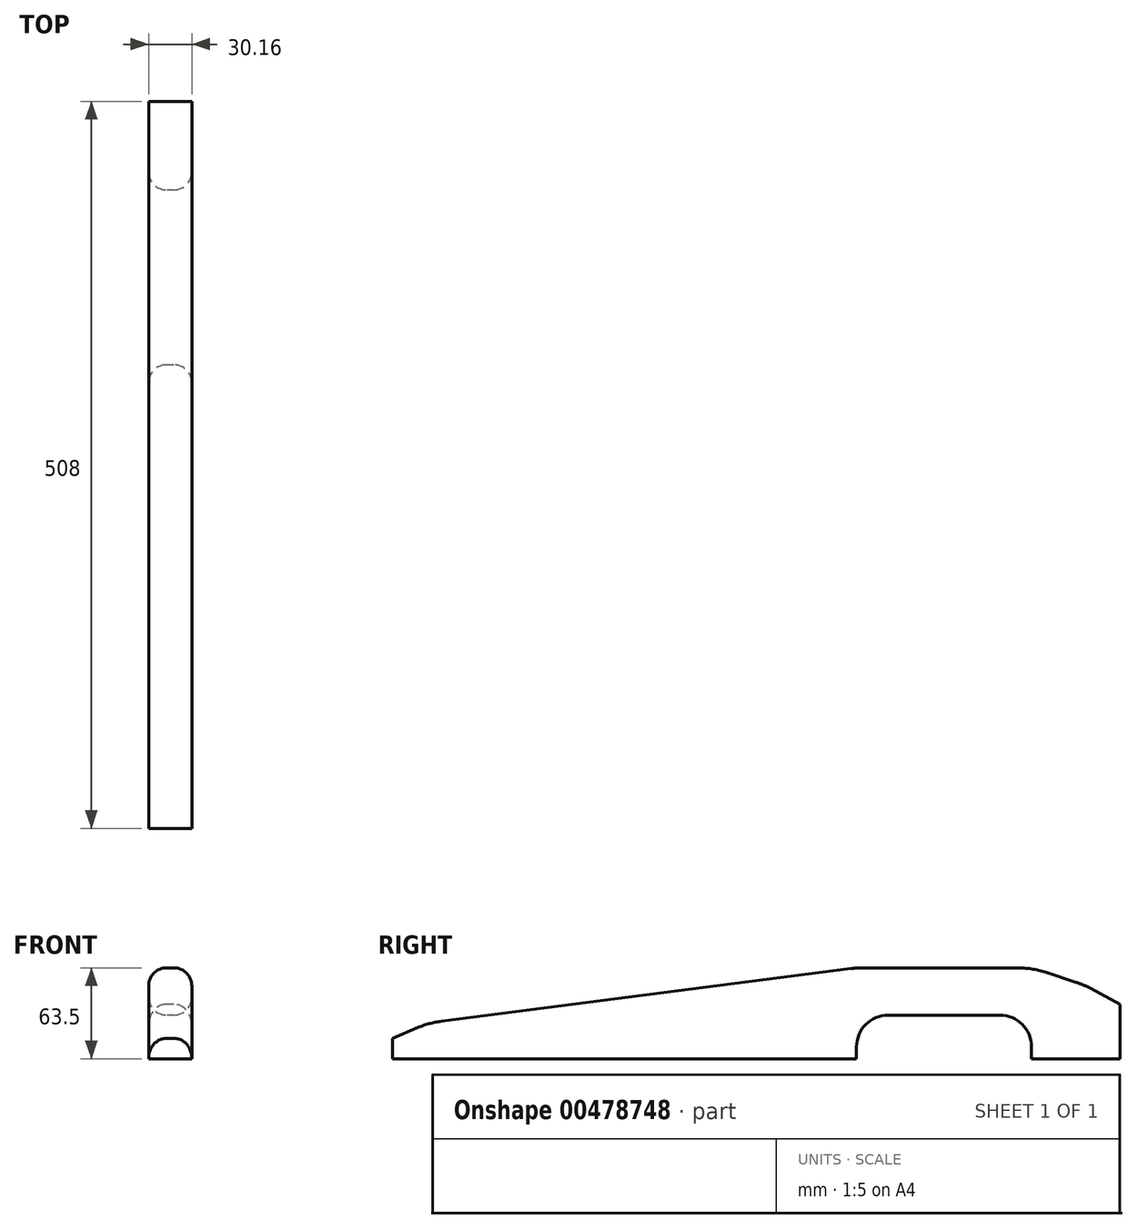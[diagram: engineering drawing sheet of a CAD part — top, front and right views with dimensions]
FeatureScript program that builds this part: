
annotation { "Feature Type Name" : "Feature", "Feature Type Description" : "" }
export const myFeature = defineFeature(function(context is Context, id is Id, definition is map)
    precondition{}
    {
        {
            var Q0;
            Q0=qCreatedBy(makeId("Right.planeOp"),FACE);
            var sketch = newSketch(context, id + "F0", { "sketchPlane" : qUnion([Q0])});
            skLineSegment(sketch, "E0.bottom", {"start": v(0, 0) * mm, "end": v(323.85, 0) * mm});
            skLineSegment(sketch, "E0.top", {"start": v(323.85, 63.5) * mm, "end": v(446.09, 63.5) * mm});
            skLineSegment(sketch, "E0.left", {"start": v(0, 0) * mm, "end": v(0, 14.29) * mm});
            skLineSegment(sketch, "E0.right", {"start": v(508, 0) * mm, "end": v(508, 38.1) * mm});
            skPoint(sketch, "E1", {"position": v(323.85, 0) * mm});
            skPoint(sketch, "E2", {"position": v(446.09, 0) * mm});
            skPoint(sketch, "E3", {"position": v(508, 38.1) * mm});
            skPoint(sketch, "E4", {"position": v(0, 14.29) * mm});
            skLineSegment(sketch, "E5", {"start": v(323.85, 0) * mm, "end": v(323.85, 30.48) * mm});
            skLineSegment(sketch, "E6", {"start": v(323.85, 30.48) * mm, "end": v(446.09, 30.48) * mm});
            skLineSegment(sketch, "E7", {"start": v(446.09, 30.48) * mm, "end": v(446.09, 0) * mm});
            skLineSegment(sketch, "E8.trimOffspring", {"start": v(446.09, 0) * mm, "end": v(508, 0) * mm});
            skLineSegment(sketch, "E9", {"start": v(0, 14.29) * mm, "end": v(25.4, 25.07) * mm});
            skLineSegment(sketch, "E10", {"start": v(25.4, 25.07) * mm, "end": v(323.85, 63.5) * mm});
            skLineSegment(sketch, "E11", {"start": v(508, 38.1) * mm, "end": v(482.6, 51.6) * mm});
            skLineSegment(sketch, "E12", {"start": v(482.6, 51.6) * mm, "end": v(446.09, 63.5) * mm});
            skSolve(sketch);
        }
        {
            var Q0;
            Q0=makeQuery(id+"F0.imprint","IMPRINT",FACE,{"disambiguationData":[TD([[makeQuery(id+"F0.imprint","IMPRINT",EDGE,{"derivedFrom":sQuery(id+"F0.wireOp",EDGE,"E0.bottom")}),1.0]])]});
            extrude(context, id + "F1", {"entities" : qUnion([Q0]), "depth" : 15.08 * mm, "hasSecondDirection" : true, "secondDirectionOppositeDirection" : true, "secondDirectionDepth" : 15.08 * mm});
        }
        {
            var Q0;
            Q0=makeQuery(id+"F1.opExtrude","SWEPT_EDGE",EDGE,{"disambiguationData":[OSD([sQuery(id+"F0.wireOp",EDGE,"E9"),sQuery(id+"F0.wireOp",EDGE,"E10")])]});
            var Q1;
            Q1=makeQuery(id+"F1.opExtrude","SWEPT_EDGE",EDGE,{"disambiguationData":[OSD([sQuery(id+"F0.wireOp",EDGE,"E0.top"),sQuery(id+"F0.wireOp",EDGE,"E10")])]});
            var Q2;
            Q2=makeQuery(id+"F1.opExtrude","SWEPT_EDGE",EDGE,{"disambiguationData":[OSD([sQuery(id+"F0.wireOp",EDGE,"E0.top"),sQuery(id+"F0.wireOp",EDGE,"E12")])]});
            var Q3;
            Q3=makeQuery(id+"F1.opExtrude","SWEPT_EDGE",EDGE,{"disambiguationData":[OSD([sQuery(id+"F0.wireOp",EDGE,"E11"),sQuery(id+"F0.wireOp",EDGE,"E12")])]});
            fillet(context, id + "F2", {"entities" : qUnion([Q0, Q1, Q2, Q3]), "radius" : 63.5 * mm, "tangentPropagation" : true, "allowEdgeOverflow" : false});
        }
        {
            var Q0;
            Q0=makeQuery(id+"F1.opExtrude","SWEPT_EDGE",EDGE,{"disambiguationData":[OSD([sQuery(id+"F0.wireOp",EDGE,"E5"),sQuery(id+"F0.wireOp",EDGE,"E6")])]});
            var Q1;
            Q1=makeQuery(id+"F1.opExtrude","SWEPT_EDGE",EDGE,{"disambiguationData":[OSD([sQuery(id+"F0.wireOp",EDGE,"E6"),sQuery(id+"F0.wireOp",EDGE,"E7")])]});
            fillet(context, id + "F3", {"entities" : qUnion([Q0, Q1]), "radius" : 22.22 * mm, "tangentPropagation" : true, "allowEdgeOverflow" : false});
        }
        {
            var Q0;
            Q0=makeQuery(id+"F1.opExtrude","CAP_EDGE",EDGE,{"disambiguationData":[OSD([sQuery(id+"F0.wireOp",EDGE,"E0.top")])],"isStart":false});
            var Q1;
            Q1=makeQuery(id+"F1.opExtrude","CAP_EDGE",EDGE,{"disambiguationData":[OSD([sQuery(id+"F0.wireOp",EDGE,"E0.top")])],"isStart":true});
            var Q2;
            Q2=makeQuery(id+"F1.opExtrude","CAP_EDGE",EDGE,{"disambiguationData":[OSD([sQuery(id+"F0.wireOp",EDGE,"E6")])],"isStart":false});
            var Q3;
            Q3=makeQuery(id+"F1.opExtrude","CAP_EDGE",EDGE,{"disambiguationData":[OSD([sQuery(id+"F0.wireOp",EDGE,"E6")])],"isStart":true});
            fillet(context, id + "F4", {"entities" : qUnion([Q0, Q1, Q2, Q3]), "radius" : 12.7 * mm, "tangentPropagation" : true, "allowEdgeOverflow" : false});
        }
    });
